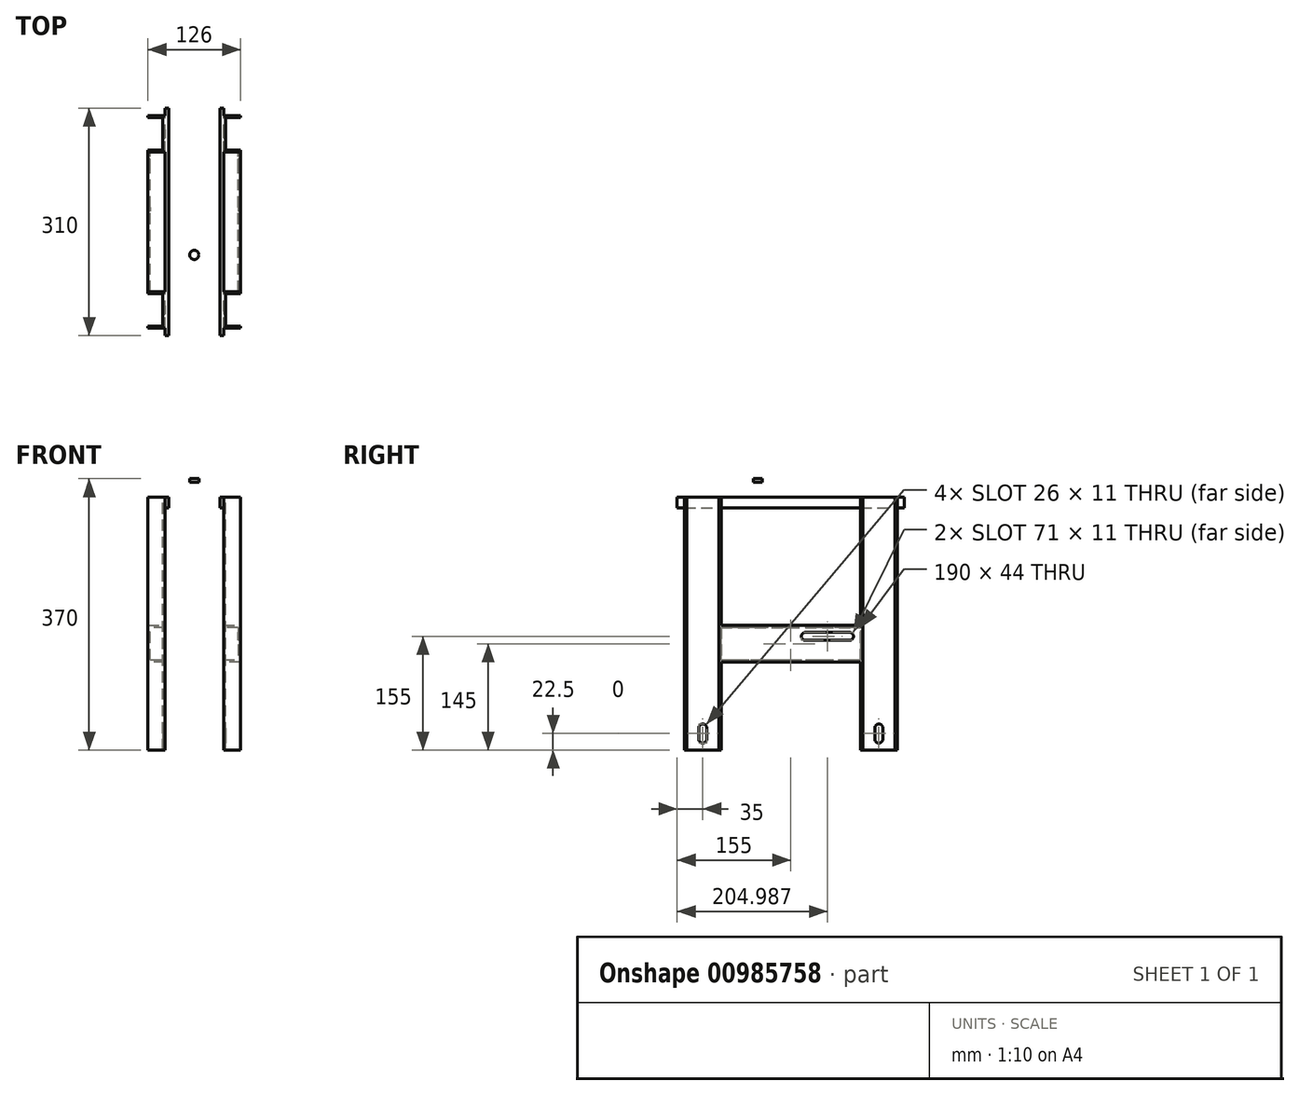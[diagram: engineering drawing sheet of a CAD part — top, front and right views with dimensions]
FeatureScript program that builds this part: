
annotation { "Feature Type Name" : "Feature", "Feature Type Description" : "" }
export const myFeature = defineFeature(function(context is Context, id is Id, definition is map)
    precondition{}
    {
        {
            var Q0;
            Q0=qCreatedBy(makeId("Front.planeOp"),FACE);
            var sketch = newSketch(context, id + "F0", { "sketchPlane" : qUnion([Q0])});
            skLineSegment(sketch, "E0.bottom", {"start": v(40, 20) * mm, "end": v(-40, 20) * mm});
            skLineSegment(sketch, "E0.top", {"start": v(40, -20) * mm, "end": v(35, -20) * mm});
            skLineSegment(sketch, "E0.left", {"start": v(40, 20) * mm, "end": v(40, -20) * mm});
            skLineSegment(sketch, "E0.right", {"start": v(-40, 20) * mm, "end": v(-40, -20) * mm});
            skPoint(sketch, "E0.middle", {"position": v(0, 0) * mm});
            skLineSegment(sketch, "E1.0", {"start": v(-35, 15) * mm, "end": v(-35, -20) * mm});
            skLineSegment(sketch, "E1.1", {"start": v(35, 15) * mm, "end": v(-35, 15) * mm});
            skLineSegment(sketch, "E1.2", {"start": v(35, 15) * mm, "end": v(35, -20) * mm});
            skLineSegment(sketch, "E2.trimOffspring", {"start": v(-35, -20) * mm, "end": v(-40, -20) * mm});
            skSolve(sketch);
        }
        {
            var Q0;
            Q0 = qSketchRegion(id + "F0", true);
            extrude(context, id + "F1", {"entities" : qUnion([Q0]), "endBound" : BoundingType.SYMMETRIC, "depth" : 310 * mm, "offsetDistance" : 25 * mm});
        }
        {
            var Q0;
            Q0=makeQuery(id+"F1.opExtrude","SWEPT_FACE",FACE,{"disambiguationData":[OSD([sQuery(id+"F0.wireOp",EDGE,"E0.bottom")])]});
            var sketch = newSketch(context, id + "F2", { "sketchPlane" : qUnion([Q0])});
            skLineSegment(sketch, "E3", {"start": v(-63, 145) * mm, "end": v(-40, 145) * mm});
            skLineSegment(sketch, "E4", {"start": v(-40, 145) * mm, "end": v(-40, 95) * mm});
            skLineSegment(sketch, "E5", {"start": v(-40, 95) * mm, "end": v(-43, 95) * mm});
            skLineSegment(sketch, "E6", {"start": v(-43, 97.99) * mm, "end": v(-43, 142) * mm});
            skLineSegment(sketch, "E7", {"start": v(-43, 142) * mm, "end": v(-63, 142) * mm});
            skLineSegment(sketch, "E8", {"start": v(-63, 142) * mm, "end": v(-63, 145) * mm});
            skLineSegment(sketch, "E9.MirrorCS", {"start": v(40, 95) * mm, "end": v(43, 95) * mm});
            skLineSegment(sketch, "E10.MirrorCS", {"start": v(63, 142) * mm, "end": v(63, 145) * mm});
            skLineSegment(sketch, "E11.MirrorCS", {"start": v(43, 97.99) * mm, "end": v(43, 142) * mm});
            skLineSegment(sketch, "E12.MirrorCS", {"start": v(43, 142) * mm, "end": v(63, 142) * mm});
            skLineSegment(sketch, "E13.MirrorCS", {"start": v(40, 145) * mm, "end": v(40, 95) * mm});
            skLineSegment(sketch, "E14.MirrorCS", {"start": v(63, 145) * mm, "end": v(40, 145) * mm});
            skLineSegment(sketch, "E15.MirrorCS", {"start": v(63, -142) * mm, "end": v(63, -145) * mm});
            skLineSegment(sketch, "E16.MirrorCS", {"start": v(-40, -95) * mm, "end": v(-43, -95) * mm});
            skLineSegment(sketch, "E17.MirrorCS", {"start": v(-63, -142) * mm, "end": v(-63, -145) * mm});
            skLineSegment(sketch, "E18.MirrorCS", {"start": v(40, -95) * mm, "end": v(43, -95) * mm});
            skLineSegment(sketch, "E19.MirrorCS", {"start": v(-43, -142) * mm, "end": v(-63, -142) * mm});
            skLineSegment(sketch, "E20.MirrorCS", {"start": v(-43, -97.99) * mm, "end": v(-43, -142) * mm});
            skLineSegment(sketch, "E21.MirrorCS", {"start": v(-63, -145) * mm, "end": v(-40, -145) * mm});
            skLineSegment(sketch, "E22.MirrorCS", {"start": v(63, -145) * mm, "end": v(40, -145) * mm});
            skLineSegment(sketch, "E23.MirrorCS", {"start": v(43, -142) * mm, "end": v(63, -142) * mm});
            skLineSegment(sketch, "E24.MirrorCS", {"start": v(40, -145) * mm, "end": v(40, -95) * mm});
            skLineSegment(sketch, "E25.MirrorCS", {"start": v(-40, -145) * mm, "end": v(-40, -95) * mm});
            skLineSegment(sketch, "E26.MirrorCS", {"start": v(43, -97.99) * mm, "end": v(43, -142) * mm});
            skLineSegment(sketch, "E27", {"start": v(-43, 97.99) * mm, "end": v(-63, 97.99) * mm});
            skLineSegment(sketch, "E28", {"start": v(-63, 97.99) * mm, "end": v(-63, 95) * mm});
            skLineSegment(sketch, "E29", {"start": v(-63, 95) * mm, "end": v(-43, 95) * mm});
            skLineSegment(sketch, "E30.MirrorCS", {"start": v(63, 95) * mm, "end": v(43, 95) * mm});
            skLineSegment(sketch, "E31.MirrorCS", {"start": v(43, 97.99) * mm, "end": v(63, 97.99) * mm});
            skLineSegment(sketch, "E32.MirrorCS", {"start": v(63, 97.99) * mm, "end": v(63, 95) * mm});
            skLineSegment(sketch, "E33.MirrorCS", {"start": v(63, -97.99) * mm, "end": v(63, -95) * mm});
            skLineSegment(sketch, "E34.MirrorCS", {"start": v(43, -97.99) * mm, "end": v(63, -97.99) * mm});
            skLineSegment(sketch, "E35.MirrorCS", {"start": v(63, -95) * mm, "end": v(43, -95) * mm});
            skLineSegment(sketch, "E36.MirrorCS", {"start": v(-63, -97.99) * mm, "end": v(-63, -95) * mm});
            skLineSegment(sketch, "E37.MirrorCS", {"start": v(-43, -97.99) * mm, "end": v(-63, -97.99) * mm});
            skLineSegment(sketch, "E38.MirrorCS", {"start": v(-63, -95) * mm, "end": v(-43, -95) * mm});
            skPoint(sketch, "E39.MirrorCS.end.orphan", {"position": v(43, -95) * mm});
            skPoint(sketch, "E39.MirrorCS.start.orphan", {"position": v(40, -95) * mm});
            skSolve(sketch);
        }
        {
            var Q0;
            Q0=makeQuery(id+"F2.imprint","IMPRINT",FACE,{"disambiguationData":[TD([[makeQuery(id+"F2.imprint","IMPRINT",EDGE,{"derivedFrom":sQuery(id+"F2.wireOp",EDGE,"E8")}),-1.0]])]});
            var Q1;
            Q1=makeQuery(id+"F2.imprint","IMPRINT",FACE,{"disambiguationData":[TD([[makeQuery(id+"F2.imprint","IMPRINT",EDGE,{"derivedFrom":sQuery(id+"F2.wireOp",EDGE,"E17.MirrorCS")}),1.0]])]});
            var Q2;
            Q2=makeQuery(id+"F2.imprint","IMPRINT",FACE,{"disambiguationData":[TD([[makeQuery(id+"F2.imprint","IMPRINT",EDGE,{"derivedFrom":sQuery(id+"F2.wireOp",EDGE,"E15.MirrorCS")}),-1.0]])]});
            var Q3;
            Q3=makeQuery(id+"F2.imprint","IMPRINT",FACE,{"disambiguationData":[TD([[makeQuery(id+"F2.imprint","IMPRINT",EDGE,{"derivedFrom":sQuery(id+"F2.wireOp",EDGE,"E10.MirrorCS")}),1.0]])]});
            extrude(context, id + "F3", {"entities" : qUnion([Q0, Q1, Q2, Q3]), "operationType" : NewBodyOperationType.ADD, "oppositeDirection" : true, "depth" : 370 * mm, "offsetDistance" : 25 * mm});
        }
        {
            var Q0;
            Q0=qCreatedBy(makeId("Right.planeOp"),FACE);
            var sketch = newSketch(context, id + "F4", { "sketchPlane" : qUnion([Q0])});
            skArc(sketch, "E40", {"start": v(114.5, -335) * mm, "mid": v(120, -340.5) * mm, "end": v(125.5, -335) * mm});
            skArc(sketch, "E41", {"start": v(125.5, -320) * mm, "mid": v(120, -314.5) * mm, "end": v(114.5, -320) * mm});
            skLineSegment(sketch, "E42", {"start": v(125.5, -320) * mm, "end": v(125.5, -335) * mm});
            skLineSegment(sketch, "E43", {"start": v(114.5, -320) * mm, "end": v(114.5, -335) * mm});
            skLineSegment(sketch, "E44.MirrorCS", {"start": v(-114.5, -320) * mm, "end": v(-114.5, -335) * mm});
            skLineSegment(sketch, "E45.MirrorCS", {"start": v(-125.5, -320) * mm, "end": v(-125.5, -335) * mm});
            skArc(sketch, "E46.MirrorCS", {"start": v(-114.5, -335) * mm, "mid": v(-120, -340.5) * mm, "end": v(-125.5, -335) * mm});
            skArc(sketch, "E47.MirrorCS", {"start": v(-125.5, -320) * mm, "mid": v(-120, -314.5) * mm, "end": v(-114.5, -320) * mm});
            skSolve(sketch);
        }
        {
            var Q0;
            Q0=makeQuery(id+"F4.imprint","IMPRINT",FACE,{"disambiguationData":[TD([[makeQuery(id+"F4.imprint","IMPRINT",EDGE,{"derivedFrom":sQuery(id+"F4.wireOp",EDGE,"E40")}),1.0]])]});
            var Q1;
            Q1=makeQuery(id+"F4.imprint","IMPRINT",FACE,{"disambiguationData":[TD([[makeQuery(id+"F4.imprint","IMPRINT",EDGE,{"derivedFrom":sQuery(id+"F4.wireOp",EDGE,"E44.MirrorCS")}),-1.0]])]});
            extrude(context, id + "F5", {"entities" : qUnion([Q0, Q1]), "operationType" : NewBodyOperationType.REMOVE, "endBound" : BoundingType.SYMMETRIC, "oppositeDirection" : true, "depth" : 100 * mm, "offsetDistance" : 25 * mm});
        }
        {
            var Q0;
            Q0=makeQuery(id+"F3.boolean.opBoolean","MERGE",FACE,{"derivedFrom":[makeQuery(id+"F1.opExtrude","SWEPT_FACE",FACE,{"disambiguationData":[OSD([sQuery(id+"F0.wireOp",EDGE,"E0.bottom")])]}),makeQuery(id+"F3.opExtrude","CAP_FACE",FACE,{"disambiguationData":[OSD([sQuery(id+"F2.wireOp",EDGE,"E10.MirrorCS"),sQuery(id+"F2.wireOp",EDGE,"E9.MirrorCS"),sQuery(id+"F2.wireOp",EDGE,"2d36dd1b-af3d-4e24-89ef-49b403e4752a5.MirrorCS"),sQuery(id+"F2.wireOp",EDGE,"E14.MirrorCS"),sQuery(id+"F2.wireOp",EDGE,"2d36dd1b-af3d-4e24-89ef-49b403e4752a10.MirrorCS"),sQuery(id+"F2.wireOp",EDGE,"E12.MirrorCS")])],"isStart":true}),makeQuery(id+"F3.opExtrude","CAP_FACE",FACE,{"disambiguationData":[OSD([sQuery(id+"F2.wireOp",EDGE,"E8"),sQuery(id+"F2.wireOp",EDGE,"E5"),sQuery(id+"F2.wireOp",EDGE,"2d36dd1b-af3d-4e24-89ef-49b403e4752a4.MirrorCS"),sQuery(id+"F2.wireOp",EDGE,"E3"),sQuery(id+"F2.wireOp",EDGE,"E7"),sQuery(id+"F2.wireOp",EDGE,"2d36dd1b-af3d-4e24-89ef-49b403e4752a9.MirrorCS")])],"isStart":true}),makeQuery(id+"F3.opExtrude","CAP_FACE",FACE,{"disambiguationData":[OSD([sQuery(id+"F2.wireOp",EDGE,"E17.MirrorCS"),sQuery(id+"F2.wireOp",EDGE,"E16.MirrorCS"),sQuery(id+"F2.wireOp",EDGE,"E166.MirrorCS"),sQuery(id+"F2.wireOp",EDGE,"E21.MirrorCS"),sQuery(id+"F2.wireOp",EDGE,"E19.MirrorCS"),sQuery(id+"F2.wireOp",EDGE,"E25.MirrorCS")])],"isStart":true}),makeQuery(id+"F3.opExtrude","CAP_FACE",FACE,{"disambiguationData":[OSD([sQuery(id+"F2.wireOp",EDGE,"E15.MirrorCS"),sQuery(id+"F2.wireOp",EDGE,"E18.MirrorCS"),sQuery(id+"F2.wireOp",EDGE,"E24.MirrorCS"),sQuery(id+"F2.wireOp",EDGE,"E22.MirrorCS"),sQuery(id+"F2.wireOp",EDGE,"E26.MirrorCS"),sQuery(id+"F2.wireOp",EDGE,"E23.MirrorCS")])],"isStart":true})]});
            var sketch = newSketch(context, id + "F6", { "sketchPlane" : qUnion([Q0])});
            skCircle(sketch, "E48", {"center": v(0, 45) * mm, "radius": 6.25 * mm});
            skCircle(sketch, "E49.MirrorC", {"center": v(0, -45) * mm, "radius": 6.25 * mm});
            skSolve(sketch);
        }
        {
            var Q0;
            Q0=makeQuery(id+"F6.imprint","IMPRINT",FACE,{"disambiguationData":[TD([[makeQuery(id+"F6.imprint","IMPRINT",EDGE,{"derivedFrom":sQuery(id+"F6.wireOp",EDGE,"E48")}),1.0]])]});
            var Q1;
            Q1=makeQuery(id+"F6.imprint","IMPRINT",FACE,{"disambiguationData":[TD([[makeQuery(id+"F6.imprint","IMPRINT",EDGE,{"derivedFrom":sQuery(id+"F6.wireOp",EDGE,"E49.MirrorC")}),-1.0]])]});
            extrude(context, id + "F7", {"entities" : qUnion([Q0, Q1]), "operationType" : NewBodyOperationType.REMOVE, "oppositeDirection" : true, "depth" : 25 * mm, "offsetDistance" : 25 * mm});
        }
        {
            var Q0;
            Q0=makeQuery(id+"F3.boolean.opBoolean","MERGE",FACE,{"derivedFrom":[makeQuery(id+"F1.opExtrude","SWEPT_FACE",FACE,{"disambiguationData":[OSD([sQuery(id+"F0.wireOp",EDGE,"E0.bottom")])]}),makeQuery(id+"F3.opExtrude","CAP_FACE",FACE,{"disambiguationData":[OSD([sQuery(id+"F2.wireOp",EDGE,"E10.MirrorCS"),sQuery(id+"F2.wireOp",EDGE,"E9.MirrorCS"),sQuery(id+"F2.wireOp",EDGE,"2d36dd1b-af3d-4e24-89ef-49b403e4752a5.MirrorCS"),sQuery(id+"F2.wireOp",EDGE,"E14.MirrorCS"),sQuery(id+"F2.wireOp",EDGE,"2d36dd1b-af3d-4e24-89ef-49b403e4752a10.MirrorCS"),sQuery(id+"F2.wireOp",EDGE,"E12.MirrorCS")])],"isStart":true}),makeQuery(id+"F3.opExtrude","CAP_FACE",FACE,{"disambiguationData":[OSD([sQuery(id+"F2.wireOp",EDGE,"E8"),sQuery(id+"F2.wireOp",EDGE,"E5"),sQuery(id+"F2.wireOp",EDGE,"2d36dd1b-af3d-4e24-89ef-49b403e4752a4.MirrorCS"),sQuery(id+"F2.wireOp",EDGE,"E3"),sQuery(id+"F2.wireOp",EDGE,"E7"),sQuery(id+"F2.wireOp",EDGE,"2d36dd1b-af3d-4e24-89ef-49b403e4752a9.MirrorCS")])],"isStart":true}),makeQuery(id+"F3.opExtrude","CAP_FACE",FACE,{"disambiguationData":[OSD([sQuery(id+"F2.wireOp",EDGE,"E17.MirrorCS"),sQuery(id+"F2.wireOp",EDGE,"E16.MirrorCS"),sQuery(id+"F2.wireOp",EDGE,"E166.MirrorCS"),sQuery(id+"F2.wireOp",EDGE,"E21.MirrorCS"),sQuery(id+"F2.wireOp",EDGE,"E19.MirrorCS"),sQuery(id+"F2.wireOp",EDGE,"E25.MirrorCS")])],"isStart":true}),makeQuery(id+"F3.opExtrude","CAP_FACE",FACE,{"disambiguationData":[OSD([sQuery(id+"F2.wireOp",EDGE,"E15.MirrorCS"),sQuery(id+"F2.wireOp",EDGE,"E18.MirrorCS"),sQuery(id+"F2.wireOp",EDGE,"E24.MirrorCS"),sQuery(id+"F2.wireOp",EDGE,"E22.MirrorCS"),sQuery(id+"F2.wireOp",EDGE,"E26.MirrorCS"),sQuery(id+"F2.wireOp",EDGE,"E23.MirrorCS")])],"isStart":true})]});
            var sketch = newSketch(context, id + "F8", { "sketchPlane" : qUnion([Q0])});
            skCircle(sketch, "E50", {"center": v(-14, -145) * mm, "radius": 3 * mm});
            skCircle(sketch, "E51", {"center": v(-14, -68) * mm, "radius": 3 * mm});
            skCircle(sketch, "E52.MirrorC", {"center": v(14, -68) * mm, "radius": 3 * mm});
            skCircle(sketch, "E53.MirrorC", {"center": v(14, -145) * mm, "radius": 3 * mm});
            skCircle(sketch, "E54.MirrorC", {"center": v(14, 68) * mm, "radius": 3 * mm});
            skCircle(sketch, "E55.MirrorC", {"center": v(-14, 145) * mm, "radius": 3 * mm});
            skCircle(sketch, "E56.MirrorC", {"center": v(14, 145) * mm, "radius": 3 * mm});
            skCircle(sketch, "E57.MirrorC", {"center": v(-14, 68) * mm, "radius": 3 * mm});
            skSolve(sketch);
        }
        {
            var Q0;
            Q0=makeQuery(id+"F8.imprint","IMPRINT",FACE,{"disambiguationData":[TD([[makeQuery(id+"F8.imprint","IMPRINT",EDGE,{"derivedFrom":sQuery(id+"F8.wireOp",EDGE,"E55.MirrorC")}),-1.0]])]});
            var Q1;
            Q1=makeQuery(id+"F8.imprint","IMPRINT",FACE,{"disambiguationData":[TD([[makeQuery(id+"F8.imprint","IMPRINT",EDGE,{"derivedFrom":sQuery(id+"F8.wireOp",EDGE,"E56.MirrorC")}),1.0]])]});
            var Q2;
            Q2=makeQuery(id+"F8.imprint","IMPRINT",FACE,{"disambiguationData":[TD([[makeQuery(id+"F8.imprint","IMPRINT",EDGE,{"derivedFrom":sQuery(id+"F8.wireOp",EDGE,"E57.MirrorC")}),-1.0]])]});
            var Q3;
            Q3=makeQuery(id+"F8.imprint","IMPRINT",FACE,{"disambiguationData":[TD([[makeQuery(id+"F8.imprint","IMPRINT",EDGE,{"derivedFrom":sQuery(id+"F8.wireOp",EDGE,"E54.MirrorC")}),1.0]])]});
            var Q4;
            Q4=makeQuery(id+"F8.imprint","IMPRINT",FACE,{"disambiguationData":[TD([[makeQuery(id+"F8.imprint","IMPRINT",EDGE,{"derivedFrom":sQuery(id+"F8.wireOp",EDGE,"E51")}),1.0]])]});
            var Q5;
            Q5=makeQuery(id+"F8.imprint","IMPRINT",FACE,{"disambiguationData":[TD([[makeQuery(id+"F8.imprint","IMPRINT",EDGE,{"derivedFrom":sQuery(id+"F8.wireOp",EDGE,"E52.MirrorC")}),-1.0]])]});
            var Q6;
            Q6=makeQuery(id+"F8.imprint","IMPRINT",FACE,{"disambiguationData":[TD([[makeQuery(id+"F8.imprint","IMPRINT",EDGE,{"derivedFrom":sQuery(id+"F8.wireOp",EDGE,"E50")}),1.0]])]});
            var Q7;
            Q7=makeQuery(id+"F8.imprint","IMPRINT",FACE,{"disambiguationData":[TD([[makeQuery(id+"F8.imprint","IMPRINT",EDGE,{"derivedFrom":sQuery(id+"F8.wireOp",EDGE,"E53.MirrorC")}),-1.0]])]});
            extrude(context, id + "F9", {"entities" : qUnion([Q0, Q1, Q2, Q3, Q4, Q5, Q6, Q7]), "operationType" : NewBodyOperationType.REMOVE, "oppositeDirection" : true, "depth" : 25 * mm, "offsetDistance" : 25 * mm});
        }
        {
            var Q0;
            Q0=qCreatedBy(makeId("Front.planeOp"),FACE);
            var sketch = newSketch(context, id + "F10", { "sketchPlane" : qUnion([Q0])});
            skLineSegment(sketch, "E58.left", {"start": v(-63, -180) * mm, "end": v(-63, -230) * mm});
            skLineSegment(sketch, "E59", {"start": v(-40, -180) * mm, "end": v(-63, -180) * mm});
            skLineSegment(sketch, "E60", {"start": v(-40, -180) * mm, "end": v(-40, -183) * mm});
            skLineSegment(sketch, "E61", {"start": v(-60, -183) * mm, "end": v(-40, -183) * mm});
            skLineSegment(sketch, "E62", {"start": v(-60, -183) * mm, "end": v(-60, -227) * mm});
            skLineSegment(sketch, "E63", {"start": v(-40, -227) * mm, "end": v(-60, -227) * mm});
            skLineSegment(sketch, "E64", {"start": v(-40, -227) * mm, "end": v(-40, -230) * mm});
            skLineSegment(sketch, "E65", {"start": v(-63, -230) * mm, "end": v(-40, -230) * mm});
            skLineSegment(sketch, "E66.MirrorCS", {"start": v(40, -180) * mm, "end": v(40, -183) * mm});
            skLineSegment(sketch, "E67.MirrorCS", {"start": v(40, -227) * mm, "end": v(40, -230) * mm});
            skLineSegment(sketch, "E68.MirrorCS", {"start": v(40, -180) * mm, "end": v(63, -180) * mm});
            skLineSegment(sketch, "E69.MirrorCS", {"start": v(60, -183) * mm, "end": v(60, -227) * mm});
            skLineSegment(sketch, "E70.MirrorCS", {"start": v(40, -227) * mm, "end": v(60, -227) * mm});
            skLineSegment(sketch, "E71.MirrorCS", {"start": v(63, -180) * mm, "end": v(63, -230) * mm});
            skLineSegment(sketch, "E72.MirrorCS", {"start": v(60, -183) * mm, "end": v(40, -183) * mm});
            skLineSegment(sketch, "E73.MirrorCS", {"start": v(63, -230) * mm, "end": v(40, -230) * mm});
            skSolve(sketch);
        }
        {
            var Q0;
            Q0=makeQuery(id+"F10.imprint","IMPRINT",FACE,{"disambiguationData":[TD([[makeQuery(id+"F10.imprint","IMPRINT",EDGE,{"derivedFrom":sQuery(id+"F10.wireOp",EDGE,"E58.left")}),-1.0]])]});
            var Q1;
            Q1=makeQuery(id+"F10.imprint","IMPRINT",FACE,{"disambiguationData":[TD([[makeQuery(id+"F10.imprint","IMPRINT",EDGE,{"derivedFrom":sQuery(id+"F10.wireOp",EDGE,"f5d9d4ac-39f7-4303-b64c-0e9c677844510.MirrorCS")}),-1.0]])]});
            var Q2;
            Q2=makeQuery(id+"F10.imprint","IMPRINT",FACE,{"disambiguationData":[TD([[makeQuery(id+"F10.imprint","IMPRINT",EDGE,{"derivedFrom":sQuery(id+"F10.wireOp",EDGE,"E58.left")}),1.0]])]});
            var Q3;
            Q3=makeQuery(id+"F10.imprint","IMPRINT",FACE,{"disambiguationData":[TD([[makeQuery(id+"F10.imprint","IMPRINT",EDGE,{"derivedFrom":sQuery(id+"F10.wireOp",EDGE,"E66.MirrorCS")}),1.0]])]});
            extrude(context, id + "F11", {"entities" : qUnion([Q0, Q1, Q2, Q3]), "operationType" : NewBodyOperationType.ADD, "endBound" : BoundingType.SYMMETRIC, "depth" : 195 * mm, "offsetDistance" : 25 * mm});
        }
        {
            var Q0;
            Q0=qCreatedBy(makeId("Right.planeOp"),FACE);
            var sketch = newSketch(context, id + "F12", { "sketchPlane" : qUnion([Q0])});
            skArc(sketch, "E74", {"start": v(79.99, -200.5) * mm, "mid": v(85.49, -195) * mm, "end": v(79.99, -189.5) * mm});
            skArc(sketch, "E75", {"start": v(19.99, -189.5) * mm, "mid": v(14.49, -195) * mm, "end": v(19.99, -200.5) * mm});
            skLineSegment(sketch, "E76", {"start": v(79.99, -189.5) * mm, "end": v(19.99, -189.5) * mm});
            skLineSegment(sketch, "E77", {"start": v(79.99, -200.5) * mm, "end": v(19.99, -200.5) * mm});
            skArc(sketch, "E78.MirrorCS", {"start": v(-79.99, -200.5) * mm, "mid": v(-85.49, -195) * mm, "end": v(-79.99, -189.5) * mm});
            skLineSegment(sketch, "E79.MirrorCS", {"start": v(-79.99, -189.5) * mm, "end": v(-19.99, -189.5) * mm});
            skLineSegment(sketch, "E80.MirrorCS", {"start": v(-79.99, -200.5) * mm, "end": v(-19.99, -200.5) * mm});
            skArc(sketch, "E81.MirrorCS", {"start": v(-19.99, -189.5) * mm, "mid": v(-14.49, -195) * mm, "end": v(-19.99, -200.5) * mm});
            skSolve(sketch);
        }
        {
            var Q0;
            Q0=makeQuery(id+"F12.imprint","IMPRINT",FACE,{"disambiguationData":[TD([[makeQuery(id+"F12.imprint","IMPRINT",EDGE,{"derivedFrom":sQuery(id+"F12.wireOp",EDGE,"E74")}),1.0]])]});
            var Q1;
            Q1=makeQuery(id+"F12.imprint","IMPRINT",FACE,{"disambiguationData":[TD([[makeQuery(id+"F12.imprint","IMPRINT",EDGE,{"derivedFrom":sQuery(id+"F12.wireOp",EDGE,"E78.MirrorCS")}),-1.0]])]});
            extrude(context, id + "F13", {"entities" : qUnion([Q0, Q1]), "operationType" : NewBodyOperationType.REMOVE, "endBound" : BoundingType.SYMMETRIC, "depth" : 150 * mm, "offsetDistance" : 25 * mm});
        }
    });
